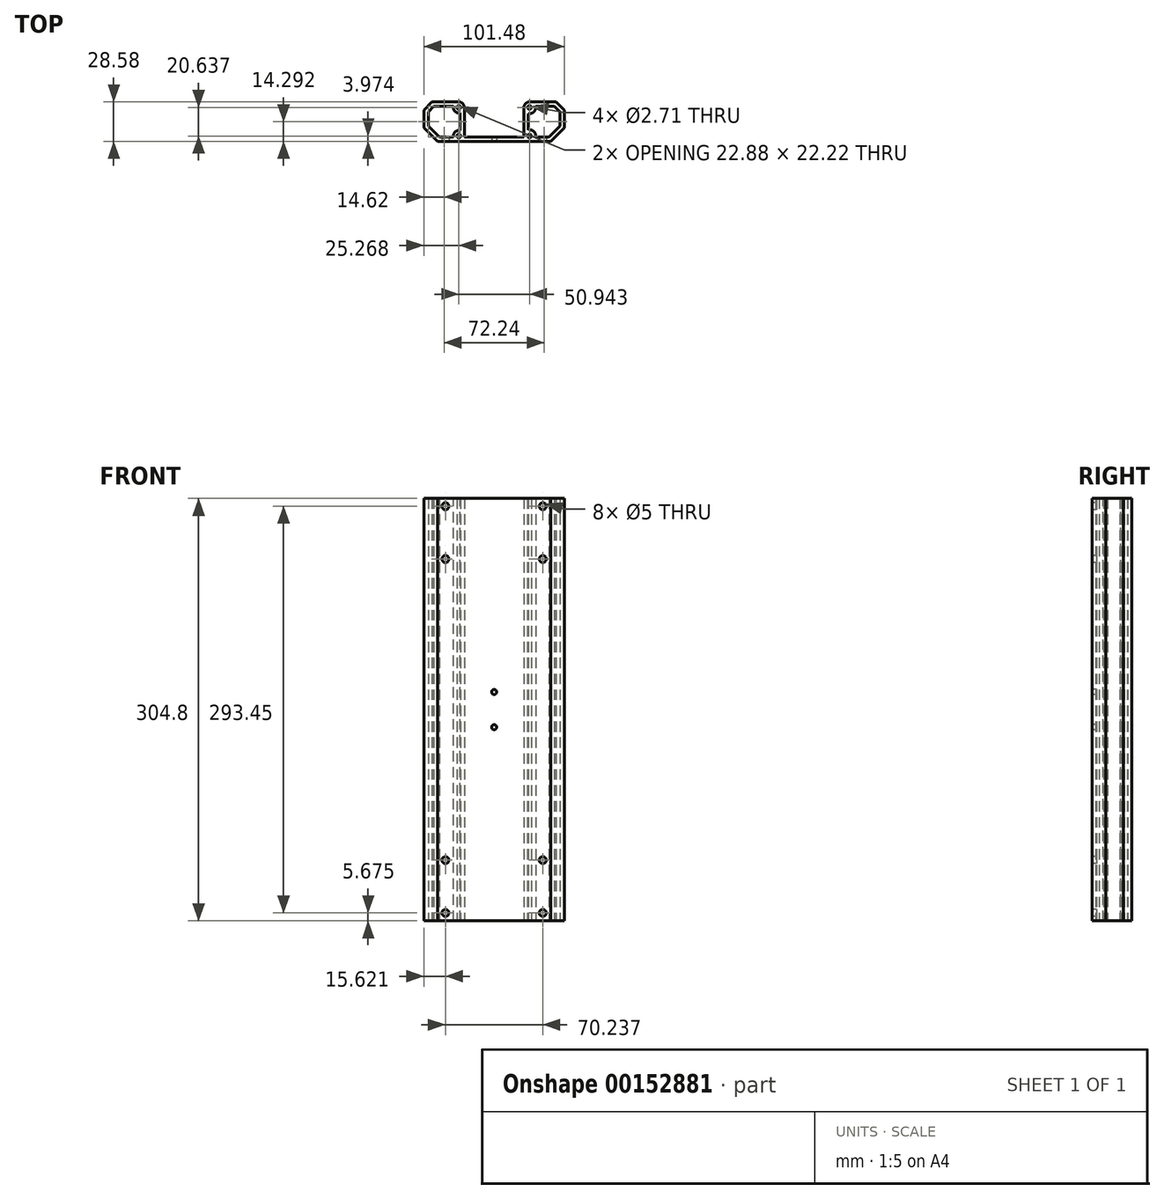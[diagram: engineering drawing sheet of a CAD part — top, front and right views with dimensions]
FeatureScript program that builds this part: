
annotation { "Feature Type Name" : "Feature", "Feature Type Description" : "" }
export const myFeature = defineFeature(function(context is Context, id is Id, definition is map)
    precondition{}
    {
        {
            var Q0;
            Q0=qCreatedBy(makeId("Top.planeOp"),FACE);
            var sketch = newSketch(context, id + "F0", { "sketchPlane" : qUnion([Q0])});
            skLineSegment(sketch, "E0.bottom", {"start": v(-21.5, 0) * mm, "end": v(21.5, 0) * mm, "construction": true});
            skLineSegment(sketch, "E0.top", {"start": v(-21.5, -25.4) * mm, "end": v(21.5, -25.4) * mm});
            skLineSegment(sketch, "E0.left", {"start": v(-21.5, 0) * mm, "end": v(-21.5, -25.4) * mm});
            skLineSegment(sketch, "E0.right", {"start": v(21.5, 0) * mm, "end": v(21.5, -25.4) * mm});
            skLineSegment(sketch, "E1", {"start": v(-21.5, 0) * mm, "end": v(-44.8, 0) * mm});
            skLineSegment(sketch, "E2", {"start": v(-25.47, 0) * mm, "end": v(-25.47, -3.97) * mm, "construction": true});
            skLineSegment(sketch, "E3", {"start": v(-25.47, -3.97) * mm, "end": v(-21.5, -3.97) * mm, "construction": true});
            skLineSegment(sketch, "E4", {"start": v(-44.8, 0) * mm, "end": v(-50.74, -5.93) * mm});
            skLineSegment(sketch, "E5", {"start": v(21.5, 0) * mm, "end": v(44.8, 0) * mm});
            skLineSegment(sketch, "E6", {"start": v(0, -25.4) * mm, "end": v(0, -28.58) * mm, "construction": true});
            skCircle(sketch, "E7", {"center": v(-25.47, -3.97) * mm, "radius": 1.35 * mm});
            skLineSegment(sketch, "E8", {"start": v(25.47, 0) * mm, "end": v(25.47, -3.97) * mm, "construction": true});
            skLineSegment(sketch, "E9", {"start": v(25.47, -3.97) * mm, "end": v(21.5, -3.97) * mm, "construction": true});
            skLineSegment(sketch, "E10", {"start": v(-40.8, -28.58) * mm, "end": v(40.8, -28.57) * mm});
            skLineSegment(sketch, "E11", {"start": v(-50.74, -5.93) * mm, "end": v(-50.74, -18.63) * mm});
            skLineSegment(sketch, "E12", {"start": v(-50.74, -18.63) * mm, "end": v(-40.8, -28.58) * mm});
            skLineSegment(sketch, "E13", {"start": v(44.8, 0) * mm, "end": v(50.74, -5.93) * mm});
            skLineSegment(sketch, "E14", {"start": v(50.74, -5.93) * mm, "end": v(50.74, -18.63) * mm});
            skLineSegment(sketch, "E15", {"start": v(50.74, -18.63) * mm, "end": v(40.8, -28.57) * mm});
            skLineSegment(sketch, "E16", {"start": v(-21.5, -24.6) * mm, "end": v(-25.47, -24.6) * mm, "construction": true});
            skLineSegment(sketch, "E17", {"start": v(-25.47, -24.6) * mm, "end": v(-25.47, -28.58) * mm, "construction": true});
            skLineSegment(sketch, "E18", {"start": v(21.5, -24.6) * mm, "end": v(25.47, -24.6) * mm, "construction": true});
            skLineSegment(sketch, "E19", {"start": v(25.47, -24.6) * mm, "end": v(25.47, -28.58) * mm, "construction": true});
            skCircle(sketch, "E20", {"center": v(-25.47, -24.6) * mm, "radius": 1.35 * mm});
            skCircle(sketch, "E21", {"center": v(25.47, -24.6) * mm, "radius": 1.35 * mm});
            skCircle(sketch, "E22", {"center": v(25.47, -3.97) * mm, "radius": 1.35 * mm});
            skLineSegment(sketch, "E23", {"start": v(0, 0) * mm, "end": v(0, -12.28) * mm, "construction": true});
            skLineSegment(sketch, "E24", {"start": v(50.74, -18.63) * mm, "end": v(40.8, -18.63) * mm, "construction": true});
            skLineSegment(sketch, "E25", {"start": v(40.8, -18.63) * mm, "end": v(40.8, -28.57) * mm, "construction": true});
            skLineSegment(sketch, "E26", {"start": v(-50.74, -12.28) * mm, "end": v(50.74, -12.28) * mm, "construction": true});
            skSolve(sketch);
        }
        {
            var Q0;
            Q0 = qSketchRegion(id + "F0", true);
            extrude(context, id + "F1", {"entities" : qUnion([Q0]), "depth" : 304.8 * mm});
        }
        {
            var Q0;
            Q0=makeQuery(id+"F1.opExtrude","CAP_FACE",FACE,{"disambiguationData":[OSD([sQuery(id+"F0.wireOp",EDGE,"E0.top"),sQuery(id+"F0.wireOp",EDGE,"E0.left"),sQuery(id+"F0.wireOp",EDGE,"E0.right"),sQuery(id+"F0.wireOp",EDGE,"E1"),sQuery(id+"F0.wireOp",EDGE,"E4"),sQuery(id+"F0.wireOp",EDGE,"E5"),sQuery(id+"F0.wireOp",EDGE,"E7"),sQuery(id+"F0.wireOp",EDGE,"E10"),sQuery(id+"F0.wireOp",EDGE,"E11"),sQuery(id+"F0.wireOp",EDGE,"E12"),sQuery(id+"F0.wireOp",EDGE,"E13"),sQuery(id+"F0.wireOp",EDGE,"E14"),sQuery(id+"F0.wireOp",EDGE,"E15"),sQuery(id+"F0.wireOp",EDGE,"E20"),sQuery(id+"F0.wireOp",EDGE,"E21"),sQuery(id+"F0.wireOp",EDGE,"E22")])],"isStart":false});
            shell(context, id + "F2", {"entities" : qUnion([Q0]), "thickness" : 3.17 * mm});
        }
        {
            var Q0;
            Q0=makeQuery(id+"F1.opExtrude","CAP_FACE",FACE,{"disambiguationData":[OSD([sQuery(id+"F0.wireOp",EDGE,"E0.top"),sQuery(id+"F0.wireOp",EDGE,"E0.left"),sQuery(id+"F0.wireOp",EDGE,"E0.right"),sQuery(id+"F0.wireOp",EDGE,"E1"),sQuery(id+"F0.wireOp",EDGE,"E4"),sQuery(id+"F0.wireOp",EDGE,"E5"),sQuery(id+"F0.wireOp",EDGE,"E7"),sQuery(id+"F0.wireOp",EDGE,"E10"),sQuery(id+"F0.wireOp",EDGE,"E11"),sQuery(id+"F0.wireOp",EDGE,"E12"),sQuery(id+"F0.wireOp",EDGE,"E13"),sQuery(id+"F0.wireOp",EDGE,"E14"),sQuery(id+"F0.wireOp",EDGE,"E15"),sQuery(id+"F0.wireOp",EDGE,"E20"),sQuery(id+"F0.wireOp",EDGE,"E21"),sQuery(id+"F0.wireOp",EDGE,"E22")])],"isStart":false});
            var sketch = newSketch(context, id + "F3", { "sketchPlane" : qUnion([Q0])});
            skArc(sketch, "E27", {"start": v(-29.44, -3.97) * mm, "mid": v(-28.28, -6.78) * mm, "end": v(-25.47, -7.94) * mm});
            skLineSegment(sketch, "E28.bottom", {"start": v(-30, -3.17) * mm, "end": v(-29.44, -3.17) * mm});
            skLineSegment(sketch, "E28.top", {"start": v(-30, -8.5) * mm, "end": v(-24.68, -8.5) * mm});
            skLineSegment(sketch, "E28.left", {"start": v(-30, -3.18) * mm, "end": v(-30, -8.5) * mm});
            skLineSegment(sketch, "E28.right", {"start": v(-24.68, -7.94) * mm, "end": v(-24.68, -8.5) * mm});
            skLineSegment(sketch, "E29", {"start": v(-29.44, -3.97) * mm, "end": v(-29.44, -3.18) * mm});
            skLineSegment(sketch, "E30", {"start": v(-25.47, -7.94) * mm, "end": v(-24.68, -7.94) * mm});
            skArc(sketch, "E31", {"start": v(-25.47, -20.64) * mm, "mid": v(-28.28, -21.8) * mm, "end": v(-29.44, -24.6) * mm});
            skLineSegment(sketch, "E32.bottom", {"start": v(-30, -25.4) * mm, "end": v(-29.44, -25.4) * mm});
            skLineSegment(sketch, "E32.top", {"start": v(-30, -20.08) * mm, "end": v(-24.68, -20.08) * mm});
            skLineSegment(sketch, "E32.left", {"start": v(-30, -25.4) * mm, "end": v(-30, -20.08) * mm});
            skLineSegment(sketch, "E32.right", {"start": v(-24.68, -20.64) * mm, "end": v(-24.68, -20.08) * mm});
            skLineSegment(sketch, "E33", {"start": v(-29.44, -25.4) * mm, "end": v(-29.44, -24.6) * mm});
            skLineSegment(sketch, "E34", {"start": v(-24.68, -20.64) * mm, "end": v(-25.47, -20.64) * mm});
            skSolve(sketch);
        }
        {
            var Q0;
            Q0 = qSketchRegion(id + "F3", true);
            var Q1;
            Q1=makeQuery(id+"F2.opShell","OFFSET_FACE",FACE,{"disambiguationData":[OSD([sQuery(id+"F0.wireOp",EDGE,"E0.top"),sQuery(id+"F0.wireOp",EDGE,"E0.left"),sQuery(id+"F0.wireOp",EDGE,"E0.right"),sQuery(id+"F0.wireOp",EDGE,"E1"),sQuery(id+"F0.wireOp",EDGE,"E4"),sQuery(id+"F0.wireOp",EDGE,"E5"),sQuery(id+"F0.wireOp",EDGE,"E7"),sQuery(id+"F0.wireOp",EDGE,"E10"),sQuery(id+"F0.wireOp",EDGE,"E11"),sQuery(id+"F0.wireOp",EDGE,"E12"),sQuery(id+"F0.wireOp",EDGE,"E13"),sQuery(id+"F0.wireOp",EDGE,"E14"),sQuery(id+"F0.wireOp",EDGE,"E15"),sQuery(id+"F0.wireOp",EDGE,"E20"),sQuery(id+"F0.wireOp",EDGE,"E21"),sQuery(id+"F0.wireOp",EDGE,"E22")]),OD(0.0)]});
            extrude(context, id + "F4", {"entities" : qUnion([Q0]), "operationType" : NewBodyOperationType.REMOVE, "endBound" : BoundingType.UP_TO_SURFACE, "oppositeDirection" : true, "endBoundEntityFace" : qUnion([Q1]), "depth" : 25.4 * mm});
        }
        {
            var Q0;
            Q0=qCreatedBy(makeId("Top.planeOp"),FACE);
            var sketch = newSketch(context, id + "F5", { "sketchPlane" : qUnion([Q0])});
            skCircle(sketch, "E35", {"center": v(0, -14.29) * mm, "radius": 3.97 * mm});
            skLineSegment(sketch, "E36.bottom", {"start": v(25.47, -3.97) * mm, "end": v(-25.47, -3.97) * mm, "construction": true});
            skLineSegment(sketch, "E36.top", {"start": v(25.47, -24.6) * mm, "end": v(-25.47, -24.6) * mm, "construction": true});
            skLineSegment(sketch, "E36.left", {"start": v(25.47, -3.97) * mm, "end": v(25.47, -24.6) * mm, "construction": true});
            skLineSegment(sketch, "E36.right", {"start": v(-25.47, -3.97) * mm, "end": v(-25.47, -24.6) * mm, "construction": true});
            skSolve(sketch);
        }
        {
            var Q0;
            Q0=makeQuery(id+"F1.opExtrude","SWEPT_EDGE",EDGE,{"disambiguationData":[OSD([sQuery(id+"F0.wireOp",EDGE,"E0.right"),sQuery(id+"F0.wireOp",EDGE,"E5")])]});
            var Q1;
            Q1=makeQuery(id+"F1.opExtrude","SWEPT_EDGE",EDGE,{"disambiguationData":[OSD([sQuery(id+"F0.wireOp",EDGE,"E0.left"),sQuery(id+"F0.wireOp",EDGE,"E1")])]});
            fillet(context, id + "F6", {"entities" : qUnion([Q0, Q1]), "radius" : 3.97 * mm, "tangentPropagation" : true, "allowEdgeOverflow" : false});
        }
        {
            var Q0;
            Q0=makeQuery(id+"F4.boolean.opBoolean","MERGE",FACE,{"derivedFrom":[makeQuery(id+"F2.opShell","OFFSET_FACE",FACE,{"disambiguationData":[OSD([sQuery(id+"F0.wireOp",EDGE,"E0.top"),sQuery(id+"F0.wireOp",EDGE,"E0.left"),sQuery(id+"F0.wireOp",EDGE,"E0.right"),sQuery(id+"F0.wireOp",EDGE,"E1"),sQuery(id+"F0.wireOp",EDGE,"E4"),sQuery(id+"F0.wireOp",EDGE,"E5"),sQuery(id+"F0.wireOp",EDGE,"E7"),sQuery(id+"F0.wireOp",EDGE,"E10"),sQuery(id+"F0.wireOp",EDGE,"E11"),sQuery(id+"F0.wireOp",EDGE,"E12"),sQuery(id+"F0.wireOp",EDGE,"E13"),sQuery(id+"F0.wireOp",EDGE,"E14"),sQuery(id+"F0.wireOp",EDGE,"E15"),sQuery(id+"F0.wireOp",EDGE,"E20"),sQuery(id+"F0.wireOp",EDGE,"E21"),sQuery(id+"F0.wireOp",EDGE,"E22")]),OD(0.0)]}),makeQuery(id+"F4.opExtrude","CAP_FACE",FACE,{"disambiguationData":[OSD([sQuery(id+"F3.wireOp",EDGE,"E27"),sQuery(id+"F3.wireOp",EDGE,"E28.bottom"),sQuery(id+"F3.wireOp",EDGE,"E28.top"),sQuery(id+"F3.wireOp",EDGE,"E28.left"),sQuery(id+"F3.wireOp",EDGE,"E28.right"),sQuery(id+"F3.wireOp",EDGE,"E29"),sQuery(id+"F3.wireOp",EDGE,"E30")])],"isStart":false}),makeQuery(id+"F4.opExtrude","CAP_FACE",FACE,{"disambiguationData":[OSD([sQuery(id+"F3.wireOp",EDGE,"E31"),sQuery(id+"F3.wireOp",EDGE,"E32.bottom"),sQuery(id+"F3.wireOp",EDGE,"E32.top"),sQuery(id+"F3.wireOp",EDGE,"E32.left"),sQuery(id+"F3.wireOp",EDGE,"E32.right"),sQuery(id+"F3.wireOp",EDGE,"E33"),sQuery(id+"F3.wireOp",EDGE,"E34")])],"isStart":false})]});
            var Q1;
            Q1=makeQuery(id+"Fm84gx8RC0MeIDj_1.1.F4.boolean.opBoolean","MERGE",FACE,{"derivedFrom":[makeQuery(id+"F2.opShell","OFFSET_FACE",FACE,{"disambiguationData":[OSD([sQuery(id+"F0.wireOp",EDGE,"E0.top"),sQuery(id+"F0.wireOp",EDGE,"E0.left"),sQuery(id+"F0.wireOp",EDGE,"E0.right"),sQuery(id+"F0.wireOp",EDGE,"E1"),sQuery(id+"F0.wireOp",EDGE,"E4"),sQuery(id+"F0.wireOp",EDGE,"E5"),sQuery(id+"F0.wireOp",EDGE,"E7"),sQuery(id+"F0.wireOp",EDGE,"E10"),sQuery(id+"F0.wireOp",EDGE,"E11"),sQuery(id+"F0.wireOp",EDGE,"E12"),sQuery(id+"F0.wireOp",EDGE,"E13"),sQuery(id+"F0.wireOp",EDGE,"E14"),sQuery(id+"F0.wireOp",EDGE,"E15"),sQuery(id+"F0.wireOp",EDGE,"E20"),sQuery(id+"F0.wireOp",EDGE,"E21"),sQuery(id+"F0.wireOp",EDGE,"E22")]),OD(1.0)]}),makeQuery(id+"Fm84gx8RC0MeIDj_1.1.F4.opExtrude","CAP_FACE",FACE,{"disambiguationData":[OSD([sQuery(id+"F3.wireOp",EDGE,"E27"),sQuery(id+"F3.wireOp",EDGE,"E28.bottom"),sQuery(id+"F3.wireOp",EDGE,"E28.top"),sQuery(id+"F3.wireOp",EDGE,"E28.left"),sQuery(id+"F3.wireOp",EDGE,"E28.right"),sQuery(id+"F3.wireOp",EDGE,"E29"),sQuery(id+"F3.wireOp",EDGE,"E30")])],"isStart":false}),makeQuery(id+"Fm84gx8RC0MeIDj_1.1.F4.opExtrude","CAP_FACE",FACE,{"disambiguationData":[OSD([sQuery(id+"F3.wireOp",EDGE,"E31"),sQuery(id+"F3.wireOp",EDGE,"E32.bottom"),sQuery(id+"F3.wireOp",EDGE,"E32.top"),sQuery(id+"F3.wireOp",EDGE,"E32.left"),sQuery(id+"F3.wireOp",EDGE,"E32.right"),sQuery(id+"F3.wireOp",EDGE,"E33"),sQuery(id+"F3.wireOp",EDGE,"E34")])],"isStart":false})]});
            var Q2;
            Q2=makeQuery(id+"F1.opExtrude","CAP_FACE",FACE,{"disambiguationData":[OSD([sQuery(id+"F0.wireOp",EDGE,"E0.top"),sQuery(id+"F0.wireOp",EDGE,"E0.left"),sQuery(id+"F0.wireOp",EDGE,"E0.right"),sQuery(id+"F0.wireOp",EDGE,"E1"),sQuery(id+"F0.wireOp",EDGE,"E4"),sQuery(id+"F0.wireOp",EDGE,"E5"),sQuery(id+"F0.wireOp",EDGE,"E7"),sQuery(id+"F0.wireOp",EDGE,"E10"),sQuery(id+"F0.wireOp",EDGE,"E11"),sQuery(id+"F0.wireOp",EDGE,"E12"),sQuery(id+"F0.wireOp",EDGE,"E13"),sQuery(id+"F0.wireOp",EDGE,"E14"),sQuery(id+"F0.wireOp",EDGE,"E15"),sQuery(id+"F0.wireOp",EDGE,"E20"),sQuery(id+"F0.wireOp",EDGE,"E21"),sQuery(id+"F0.wireOp",EDGE,"E22")])],"isStart":true});
            extrude(context, id + "F7", {"entities" : qUnion([Q0, Q1]), "operationType" : NewBodyOperationType.REMOVE, "endBound" : BoundingType.UP_TO_SURFACE, "oppositeDirection" : true, "endBoundEntityFace" : qUnion([Q2]), "depth" : 25.4 * mm});
        }
        {
            var Q0;
            Q0=makeQuery(id+"F1.opExtrude","SWEPT_FACE",FACE,{"disambiguationData":[OSD([sQuery(id+"F0.wireOp",EDGE,"E10")])]});
            var sketch = newSketch(context, id + "F8", { "sketchPlane" : qUnion([Q0])});
            skLineSegment(sketch, "E37", {"start": v(0, 304.8) * mm, "end": v(0, 0) * mm, "construction": true});
            skLineSegment(sketch, "E38.bottom", {"start": v(35.12, 299.12) * mm, "end": v(-35.12, 299.12) * mm, "construction": true});
            skLineSegment(sketch, "E38.top", {"start": v(35.12, 261.02) * mm, "end": v(-35.12, 261.02) * mm, "construction": true});
            skLineSegment(sketch, "E38.left", {"start": v(35.12, 299.13) * mm, "end": v(35.12, 261.02) * mm, "construction": true});
            skLineSegment(sketch, "E38.right", {"start": v(-35.12, 299.12) * mm, "end": v(-35.12, 261.02) * mm, "construction": true});
            skPoint(sketch, "E38.middle", {"position": v(0, 280.07) * mm});
            skLineSegment(sketch, "E39.bottom", {"start": v(35.12, 299.12) * mm, "end": v(40.8, 299.12) * mm, "construction": true});
            skLineSegment(sketch, "E39.top", {"start": v(35.12, 304.8) * mm, "end": v(40.8, 304.8) * mm, "construction": true});
            skLineSegment(sketch, "E39.left", {"start": v(35.12, 299.13) * mm, "end": v(35.12, 304.8) * mm, "construction": true});
            skLineSegment(sketch, "E39.right", {"start": v(40.8, 299.13) * mm, "end": v(40.8, 304.8) * mm, "construction": true});
            skCircle(sketch, "E40", {"center": v(35.12, 299.13) * mm, "radius": 2.5 * mm});
            skCircle(sketch, "E41", {"center": v(-35.12, 299.12) * mm, "radius": 2.5 * mm});
            skCircle(sketch, "E42", {"center": v(-35.12, 261.02) * mm, "radius": 2.5 * mm});
            skCircle(sketch, "E43", {"center": v(35.12, 261.02) * mm, "radius": 2.5 * mm});
            skLineSegment(sketch, "E44.bottom", {"start": v(35.12, 5.68) * mm, "end": v(-35.12, 5.68) * mm, "construction": true});
            skLineSegment(sketch, "E44.top", {"start": v(35.12, 43.77) * mm, "end": v(-35.12, 43.77) * mm, "construction": true});
            skLineSegment(sketch, "E44.left", {"start": v(35.12, 5.67) * mm, "end": v(35.12, 43.77) * mm, "construction": true});
            skLineSegment(sketch, "E44.right", {"start": v(-35.12, 5.67) * mm, "end": v(-35.12, 43.77) * mm, "construction": true});
            skPoint(sketch, "E44.middle", {"position": v(0, 24.72) * mm});
            skLineSegment(sketch, "E45.bottom", {"start": v(35.12, 5.68) * mm, "end": v(40.8, 5.68) * mm, "construction": true});
            skLineSegment(sketch, "E45.top", {"start": v(35.12, 0) * mm, "end": v(40.8, 0) * mm, "construction": true});
            skLineSegment(sketch, "E45.left", {"start": v(35.12, 5.68) * mm, "end": v(35.12, 0) * mm, "construction": true});
            skLineSegment(sketch, "E45.right", {"start": v(40.8, 5.68) * mm, "end": v(40.8, 0) * mm, "construction": true});
            skCircle(sketch, "E46", {"center": v(-35.12, 43.77) * mm, "radius": 2.5 * mm});
            skCircle(sketch, "E47", {"center": v(-35.12, 5.67) * mm, "radius": 2.5 * mm});
            skCircle(sketch, "E48", {"center": v(35.12, 5.68) * mm, "radius": 2.5 * mm});
            skCircle(sketch, "E49", {"center": v(35.12, 43.77) * mm, "radius": 2.5 * mm});
            skSolve(sketch);
        }
        {
            var Q0;
            Q0 = qSketchRegion(id + "F8", true);
            var Q1;
            Q1=makeQuery(id+"F1.opExtrude","SWEPT_FACE",FACE,{"disambiguationData":[OSD([sQuery(id+"F0.wireOp",EDGE,"E0.top")])]});
            extrude(context, id + "F9", {"entities" : qUnion([Q0]), "operationType" : NewBodyOperationType.REMOVE, "endBound" : BoundingType.UP_TO_SURFACE, "oppositeDirection" : true, "endBoundEntityFace" : qUnion([Q1]), "depth" : 25.4 * mm});
        }
        {
            var Q0;
            Q0=makeQuery(id+"F1.opExtrude","SWEPT_FACE",FACE,{"disambiguationData":[OSD([sQuery(id+"F0.wireOp",EDGE,"E10")])]});
            var sketch = newSketch(context, id + "F10", { "sketchPlane" : qUnion([Q0])});
            skLineSegment(sketch, "E50", {"start": v(0, 0) * mm, "end": v(0, 139.7) * mm, "construction": true});
            skPoint(sketch, "E50.endSnap0", {"position": v(0, 0) * mm});
            skLineSegment(sketch, "E51", {"start": v(0, 139.7) * mm, "end": v(0, 165.1) * mm, "construction": true});
            skLineSegment(sketch, "E52", {"start": v(0, 165.1) * mm, "end": v(0, 304.8) * mm, "construction": true});
            skCircle(sketch, "E53", {"center": v(0, 139.7) * mm, "radius": 1.83 * mm});
            skCircle(sketch, "E54", {"center": v(0, 165.1) * mm, "radius": 1.83 * mm});
            skSolve(sketch);
        }
        {
            var Q0;
            Q0 = qSketchRegion(id + "F10", true);
            var Q1;
            Q1=makeQuery(id+"F1.opExtrude","SWEPT_FACE",FACE,{"disambiguationData":[OSD([sQuery(id+"F0.wireOp",EDGE,"E0.top")])]});
            extrude(context, id + "F11", {"entities" : qUnion([Q0]), "operationType" : NewBodyOperationType.REMOVE, "endBound" : BoundingType.UP_TO_SURFACE, "oppositeDirection" : true, "endBoundEntityFace" : qUnion([Q1]), "depth" : 25.4 * mm});
        }
    });
